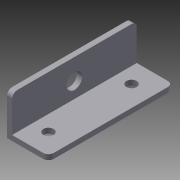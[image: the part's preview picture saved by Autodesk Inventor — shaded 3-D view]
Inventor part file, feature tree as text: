
AUTODESK INVENTOR PART (.ipt)
format: ipt  version: 2012 (Build 160160000, 160)  size: 107,520 bytes
history: native  units: in
note: dims shown in document units (in); Inventor stores cm internally (conversion verified against a paired STEP export)
features: extrude x3, sketch x3, fillet x1
ambient origin geometry x8: Origin, YZ Plane, XZ Plane, XY Plane, X Axis, Y Axis, Z Axis, Center Point
bodies: Solid1 (feature_tree)
feature tree (7):
  extrude  "Extrusion1"  Depth=0.125in
  fillet  "Fillet1"  Radius=1.0in
  extrude  "Extrusion2"  Depth=3.0in TaperAngle=0.0deg
  extrude  "Extrusion3"  Depth=0.375in
  sketch  "Sketch1"  dims[d0=0.125in d1=0.125in d2=1.0in]
  sketch  "Sketch2"  dims[d3=1.0in d4=3.0in d5=0.0in]
  sketch  "Sketch3"  dims[d6=0.125in d7=0.375in d8=4.0in d9=0.0in d10=0.5in d11=0.25in d12=0.25in d13=4.0in d14=0.0in]
